# Revit family: 01662195
name_source: partatom
category: Plumbing Fixtures
revit_build: Autodesk Revit 2016 (Build: 20150714_1515(x64)
units: mm (PartAtom-declared; Revit-internal decimal feet)

## family parameters
Always vertical = Yes
Cut with Voids When Loaded = No
OmniClass Number = 23.45.55.00
OmniClass Title = Sanitary Faucets, Wastes
Part Type = Normal
Room Calculation Point = No
Round Connector Dimension = Use Diameter
Shared = No
Work Plane-Based = No

## types (1)
- 01662195 Washbasin faucet
    2D/3D/BIM Files URL = http://static.hansa.com
    Advanced Features = Waterways without nickel coating;Low lead <0.3; Disinfection proof (max. +95°C);DZR brass; Without draw-rod opening
    Aerator = Laminar; HONEYCOMB
    AssetType = Fixed
    BIMObjectName = 01662195
    BodyMaterial = Brass
    Brand = Hansa
    Catalog Drawing URL = http://static.hansa.com
    Category = Health care
    Class = Single lever
    CloseOffRating = 0
    Color = Chrome
    Comfort Sales Arguments = Quick and easy to clean.
    Connection Size = Ø10
    ConvergoRefNr = 0087-1710-0029-DE
    Customs Code = 84818011
    DN Size = DN15
    Dimension Drawing URL = http://static.hansa.com
    Diverter = Integrated diverter / automatic reset
    DurationUnit = Year
    EAN Number = 4015474293960
    Extensions = No pop-up waste included
    FDV Document URL = http://www.hansa.com
    FaucetMainMaterial = Brass
    FaucetNominalDepth = 178 mm  [stored 0.58399 ft]
    FaucetNominalHeight = 210 mm  [stored 0.688976 ft]
    FaucetNominalWidth = 58 mm  [stored 0.190289 ft]
    Features = Laminar flow, disinfection proof (max. +95°C)
    Finish = Polished
    Flow = Laminar flow
    Flow Drawing URL = http://static.hansa.com
    Flow Rate At 300kPa = 0.2 L/s
    FlowCoefficient = 0
    Group = Washbasin faucets
    Hand Shower = Bidetta hand shower
    HandShowerNominalDepth = 64 mm  [stored 0.209974 ft]
    HandShowerNominalHeight = 338 mm
    HandShowerNominalWidth = 46 mm
    Health Sales Arguments = Brass in contact with drinking water contains less than 0.3% lead.; Surfaces in contact with drinking water do not have a nickel coating.
    IfcExportAs = IfcValveType
    IfcExportType = FAUCET
    InletConnectionSize = 10 mm  [stored 0.0328084 ft]
    Installation Type = Deck mounted
    Installation and Maintenance = http://static.hansa.com
    Lever Handle = Long lever; Loop lever; Lever with H+C symbol
    Long Marketing = One hole washbasin faucet with disinfection wash proof multifunctional shower set. Firm long lever offers good usability to all users and situations. Fixed spout and laminar flow. Shower hose 1.5 m, wall bracket, two pairs of quick-release couplings. Special flexible connection pipes with G3/8" nut.
    ManufacterURL = http://www.hansa.com
    Manufacturer = Hansa
    ManufacturerName = Hansa
    Market = AUT;BEL;CZE;DEU;ESP;FRA;INT;ITA;NLD;SVK
    Material = Brass
    Model = 01662195 Washbasin faucet
    ModelReference = 01662195
    Mounting Holes = 1 mounting hole
    NBSDescription = Water supply fittings for baths
    NBSReference = 45-35-70/315
    Name = 01662195 Washbasin faucet
    Name_en = 01662195 Washbasin faucet
    Package Weight = 3.094 kg
    Package external Dimensions = 606 x 220 x 88
    Pipes = Copper inlet pipe(s)
    Product Code = 01662195
    Product Datasheet = http://www.hansa.com
    Product Family = Hansamedipro
    Product Image URL = http://static.hansa.com
    Product URL = http://static.hansa.com
    Projection = 120 mm  [stored 0.393701 ft]
    Revision = 2
    Shape = Sculptured
    Shower Parts = Hand shower; Shower Hose (1500 mm); Shower holder
    Shower Spray = Sensitive
    Shower Spray Number = 1Spray
    Size = Faucet:58x178x210 mm / Hand shower: 46x64x338 mm
    Spare Parts = http://static.hansa.com
    Special Features = Waterways without nickel, leadfree, disinfection resistant
    Spout Type = Fixed spout
    Uniclass2 = Pr_40_30_96_78
    Uniclass2015Description = Shower manual water supply sets
    Uniclass2015Reference = Pr_40_20_87_78
    Usage Group = Toilets for disabled, pharmacies, health centers, hospitals
    Version = 2
    VersionDate = 01/01/2019
    WarrantyDescription = http://warranty.hansa.com
    WarrantyDurationUnit = Year

note: [stored X ft] marks values corroborated as IEEE doubles in the binary element streams (Revit-internal decimal feet)

## geometry (parser evidence)
native form markers: Sweep x6
no freeform markers — native parametric forms only
